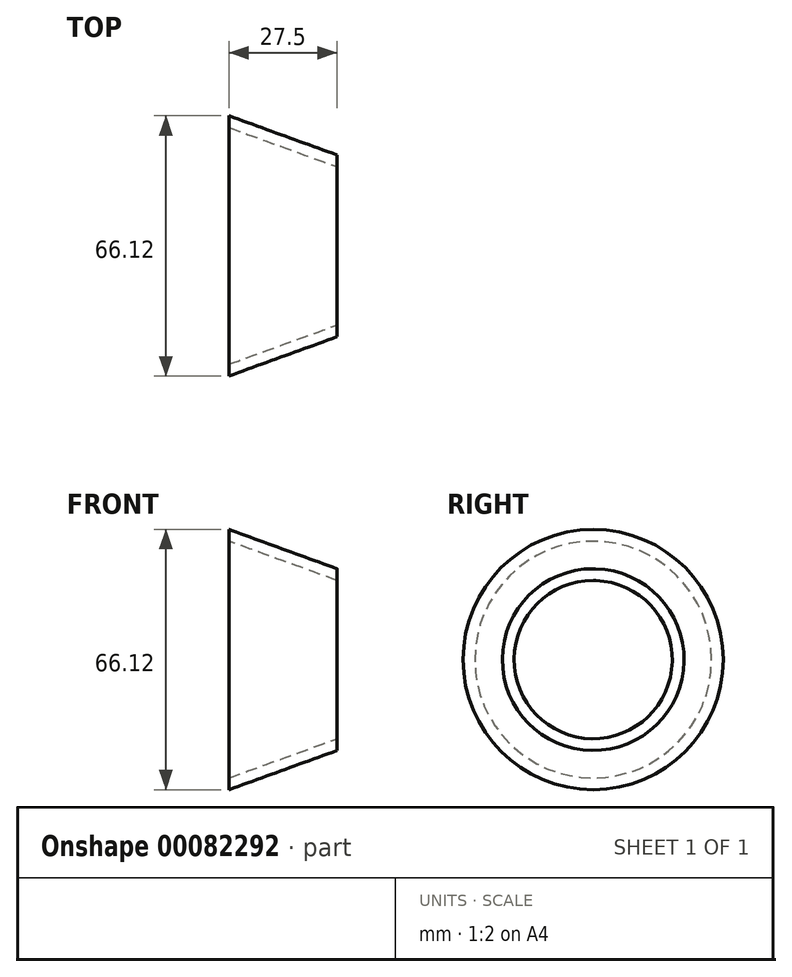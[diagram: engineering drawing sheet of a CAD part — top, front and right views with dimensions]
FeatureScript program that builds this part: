
annotation { "Feature Type Name" : "Feature", "Feature Type Description" : "" }
export const myFeature = defineFeature(function(context is Context, id is Id, definition is map)
    precondition{}
    {
        {
            var Q0;
            Q0=qCreatedBy(makeId("Right.planeOp"),FACE);
            var sketch = newSketch(context, id + "F0", { "sketchPlane" : qUnion([Q0])});
            skLineSegment(sketch, "E0", {"start": v(-27.5, 35) * mm, "end": v(-27.5, -30.86) * mm});
            skLineSegment(sketch, "E1", {"start": v(27.5, 35) * mm, "end": v(27.5, -30.86) * mm});
            skLineSegment(sketch, "E2", {"start": v(-22.5, -35.86) * mm, "end": v(22.5, -35.86) * mm});
            skPoint(sketch, "E3.orphan", {"position": v(-27.5, -21.94) * mm});
            skPoint(sketch, "E4.orphan", {"position": v(27.5, -21.94) * mm});
            skPoint(sketch, "E5.visualSharp", {"position": v(-27.5, -35.86) * mm});
            skArc(sketch, "E5.filletArc", {"start": v(-27.5, -30.86) * mm, "mid": v(-26.04, -34.4) * mm, "end": v(-22.5, -35.86) * mm});
            skPoint(sketch, "E6.visualSharp", {"position": v(27.5, -35.86) * mm});
            skArc(sketch, "E6.filletArc", {"start": v(22.5, -35.86) * mm, "mid": v(26.04, -34.4) * mm, "end": v(27.5, -30.86) * mm});
            skPoint(sketch, "E7.orphan", {"position": v(-27.5, 53.27) * mm});
            skPoint(sketch, "E8.orphan", {"position": v(27.5, 53.27) * mm});
            skLineSegment(sketch, "E9", {"start": v(-35, 35) * mm, "end": v(-35, -33.36) * mm});
            skLineSegment(sketch, "E10", {"start": v(-25, -43.36) * mm, "end": v(25, -43.36) * mm});
            skLineSegment(sketch, "E11", {"start": v(35, -33.36) * mm, "end": v(35, 35) * mm});
            skArc(sketch, "E12.filletArc", {"start": v(-35, -33.36) * mm, "mid": v(-32.07, -40.43) * mm, "end": v(-25, -43.36) * mm});
            skArc(sketch, "E13.filletArc", {"start": v(25, -43.36) * mm, "mid": v(32.07, -40.43) * mm, "end": v(35, -33.36) * mm});
            skLineSegment(sketch, "E14", {"start": v(35, 35) * mm, "end": v(-35, 35) * mm});
            skCircle(sketch, "E15", {"center": v(2, 3) * mm, "radius": 18.75 * mm});
            skSolve(sketch);
        }
        {
            var Q0;
            {var subQ2=sQuery(id+"F0.wireOp",EDGE,"E0");Q0=makeQuery(id+"F0.imprint","IMPRINT",FACE,{"disambiguationData":[TD([[makeQuery(id+"F0.imprint","IMPRINT",EDGE,{"derivedFrom":subQ2}),-1.0]])]});}
            extrude(context, id + "F1", {"entities" : qUnion([Q0]), "depth" : 7.5 * mm, "offsetDistance" : 25 * mm});
        }
        {
            var Q0;
            {var subQ0=sQuery(id+"F0.wireOp",EDGE,"E14");Q0=makeQuery(id+"F1.opExtrude","SWEPT_FACE",FACE,{"disambiguationData":[OSD([subQ0]),TDD([makeQuery(id+"F0.imprint","IMPRINT",EDGE,{"disambiguationData":[TD([[makeQuery(id+"F0.imprint","INTERSECT",VERTEX,{"derivedFrom":[sQuery(id+"F0.wireOp",EDGE,"E1"),subQ0]}),1.0]])],"derivedFrom":subQ0})])]});}
            var sketch = newSketch(context, id + "F2", { "sketchPlane" : qUnion([Q0])});
            skLineSegment(sketch, "E16.bottom", {"start": v(4.98, 27.5) * mm, "end": v(2.38, 27.5) * mm});
            skLineSegment(sketch, "E16.top", {"start": v(4.97, 32.25) * mm, "end": v(2.37, 32.25) * mm});
            skLineSegment(sketch, "E16.left", {"start": v(4.98, 27.5) * mm, "end": v(4.97, 32.25) * mm});
            skLineSegment(sketch, "E16.right", {"start": v(2.38, 27.5) * mm, "end": v(2.37, 32.25) * mm});
            skSolve(sketch);
        }
        {
            var Q0;
            Q0=makeQuery(id+"F2.imprint","IMPRINT",FACE,{"disambiguationData":[TD([[makeQuery(id+"F2.imprint","IMPRINT",EDGE,{"derivedFrom":sQuery(id+"F2.wireOp",EDGE,"E16.bottom")}),-1.0]])]});
            var Q1;
            Q1=sQuery(id+"F0.wireOp",EDGE,"E1");
            var Q2;
            Q2=sQuery(id+"F0.wireOp",EDGE,"E6.filletArc");
            var Q3;
            Q3=sQuery(id+"F0.wireOp",EDGE,"E2");
            var Q4;
            Q4=sQuery(id+"F0.wireOp",EDGE,"E5.filletArc");
            var Q5;
            Q5=sQuery(id+"F0.wireOp",EDGE,"E0");
            sweep(context, id + "F3", {"operationType" : NewBodyOperationType.REMOVE, "profiles" : qUnion([Q0]), "path" : qUnion([Q1, Q2, Q3, Q4, Q5])});
        }
        {
            var Q0;
            {var subQ2=sQuery(id+"F0.wireOp",EDGE,"E0");Q0=makeQuery(id+"F0.imprint","IMPRINT",FACE,{"disambiguationData":[TD([[makeQuery(id+"F0.imprint","IMPRINT",EDGE,{"derivedFrom":subQ2}),1.0]])]});}
            var Q1;
            Q1=makeQuery(id+"F0.imprint","IMPRINT",FACE,{"disambiguationData":[TD([[makeQuery(id+"F0.imprint","IMPRINT",EDGE,{"derivedFrom":sQuery(id+"F0.wireOp",EDGE,"RalXa7Zk-iRiR-DEGu-MVaw-sS2nsxJwCIpq")}),-1.0]])]});
            var Q2;
            Q2=makeQuery(id+"F0.imprint","IMPRINT",FACE,{"disambiguationData":[TD([[makeQuery(id+"F0.imprint","IMPRINT",EDGE,{"derivedFrom":sQuery(id+"F0.wireOp",EDGE,"RalXa7Zk-iRiR-DEGu-MVaw-sS2nsxJwCIpq")}),1.0]])]});
            var Q3;
            Q3=makeQuery(id+"F0.imprint","IMPRINT",FACE,{"disambiguationData":[TD([[makeQuery(id+"F0.imprint","IMPRINT",EDGE,{"derivedFrom":sQuery(id+"F0.wireOp",EDGE,"85QicEso-iMtD-wqBT-e6sD-r58lY0pxuzTS")}),1.0]])]});
            extrude(context, id + "F4", {"entities" : qUnion([Q0, Q1, Q2, Q3]), "operationType" : NewBodyOperationType.ADD, "depth" : 2.38 * mm, "offsetDistance" : 25 * mm});
        }
        {
            var Q0;
            Q0=qCreatedBy(makeId("Top.planeOp"),FACE);
            cPlane(context, id + "F5", {"entities" : qUnion([Q0]), "cplaneType" : CPlaneType.OFFSET, "offset" : 1 * mm, "width" : 150 * mm, "height" : 150 * mm});
        }
        {
            var Q0;
            Q0=qCreatedBy(id+"F5.planeOp",FACE);
            var sketch = newSketch(context, id + "F6", { "sketchPlane" : qUnion([Q0])});
            skLineSegment(sketch, "E17", {"start": v(0, 25) * mm, "end": v(-27.5, 35) * mm});
            skLineSegment(sketch, "E18", {"start": v(-27.5, 35) * mm, "end": v(-27.5, 32) * mm});
            skLineSegment(sketch, "E19", {"start": v(-27.5, 32) * mm, "end": v(0, 22) * mm});
            skLineSegment(sketch, "E20", {"start": v(0, 22) * mm, "end": v(0, 25) * mm});
            skSolve(sketch);
        }
        {
            var Q0;
            Q0=makeQuery(id+"F6.imprint","IMPRINT",FACE,{"disambiguationData":[TD([[makeQuery(id+"F6.imprint","IMPRINT",EDGE,{"derivedFrom":sQuery(id+"F6.wireOp",EDGE,"E17")}),1.0]])]});
            var Q1;
            Q1=sQuery(id+"F0.wireOp",EDGE,"E15");
            revolve(context, id + "F7", {"operationType" : NewBodyOperationType.ADD, "surfaceOperationType" : NewSurfaceOperationType.NEW, "entities" : qUnion([Q0]), "axis" : qUnion([Q1]), "revolveType" : RevolveType.FULL});
        }
        {
            var Q0;
            {var subQ0=sQuery(id+"F0.wireOp",EDGE,"E0");var subQ1=sQuery(id+"F0.wireOp",EDGE,"E14");var subQ3=sQuery(id+"F0.wireOp",EDGE,"E1");Q0=makeQuery(id+"F3.boolean.opBoolean","SPLIT",EDGE,{"disambiguationData":[TD([makeQuery(id+"F3.opSweep","SWEPT_FACE",FACE,{"disambiguationData":[OSD([subQ3,sQuery(id+"F2.wireOp",EDGE,"E16.left")])]})])],"derivedFrom":makeQuery(id+"F1.opExtrude","SWEPT_EDGE",EDGE,{"disambiguationData":[OSD([subQ0,subQ1])]})});}
            var Q1;
            {var subQ0=sQuery(id+"F0.wireOp",EDGE,"E14");var subQ2=sQuery(id+"F0.wireOp",EDGE,"E1");Q1=makeQuery(id+"F3.boolean.opBoolean","SPLIT",EDGE,{"disambiguationData":[TD([makeQuery(id+"F3.opSweep","SWEPT_FACE",FACE,{"disambiguationData":[OSD([subQ2,sQuery(id+"F2.wireOp",EDGE,"E16.left")])]})])],"derivedFrom":makeQuery(id+"F1.opExtrude","SWEPT_EDGE",EDGE,{"disambiguationData":[OSD([subQ2,subQ0])]})});}
            fillet(context, id + "F8", {"entities" : qUnion([Q0, Q1]), "tangentPropagation" : true, "radius" : 4 * mm, "defaultsChanged" : false, "vertexSettings" : [], "allowEdgeOverflow" : false});
        }
        {
            var Q0;
            Q0=makeQuery(id+"F1.opExtrude","SWEPT_FACE",FACE,{"disambiguationData":[OSD([sQuery(id+"F0.wireOp",EDGE,"E10")])]});
            var sketch = newSketch(context, id + "F9", { "sketchPlane" : qUnion([Q0])});
            skLineSegment(sketch, "E21.bottom", {"start": v(0, -46.43) * mm, "end": v(9.44, -46.43) * mm});
            skLineSegment(sketch, "E21.top", {"start": v(0, 44.81) * mm, "end": v(9.44, 44.81) * mm});
            skLineSegment(sketch, "E21.left", {"start": v(0, -46.43) * mm, "end": v(0, 44.81) * mm});
            skLineSegment(sketch, "E21.right", {"start": v(9.44, -46.43) * mm, "end": v(9.44, 44.81) * mm});
            skSolve(sketch);
        }
        {
            var Q0;
            {var subQ5=sQuery(id+"F9.wireOp",EDGE,"E21.bottom");Q0=makeQuery(id+"F9.imprint","IMPRINT",FACE,{"disambiguationData":[TD([[makeQuery(id+"F9.imprint","IMPRINT",EDGE,{"derivedFrom":subQ5}),1.0]])]});}
            var Q1;
            {var subQ1=sQuery(id+"F0.wireOp",EDGE,"E10");Q1=makeQuery(id+"F9.imprint","IMPRINT",FACE,{"disambiguationData":[TD([[makeQuery(id+"F9.imprint","IMPRINT",EDGE,{"derivedFrom":makeQuery(id+"F1.opExtrude","CAP_EDGE",EDGE,{"disambiguationData":[OSD([subQ1])],"isStart":false})}),-1.0]])]});}
            extrude(context, id + "F10", {"entities" : qUnion([Q0, Q1]), "operationType" : NewBodyOperationType.REMOVE, "oppositeDirection" : true, "depth" : 86 * mm, "offsetDistance" : 25 * mm});
        }
    });
